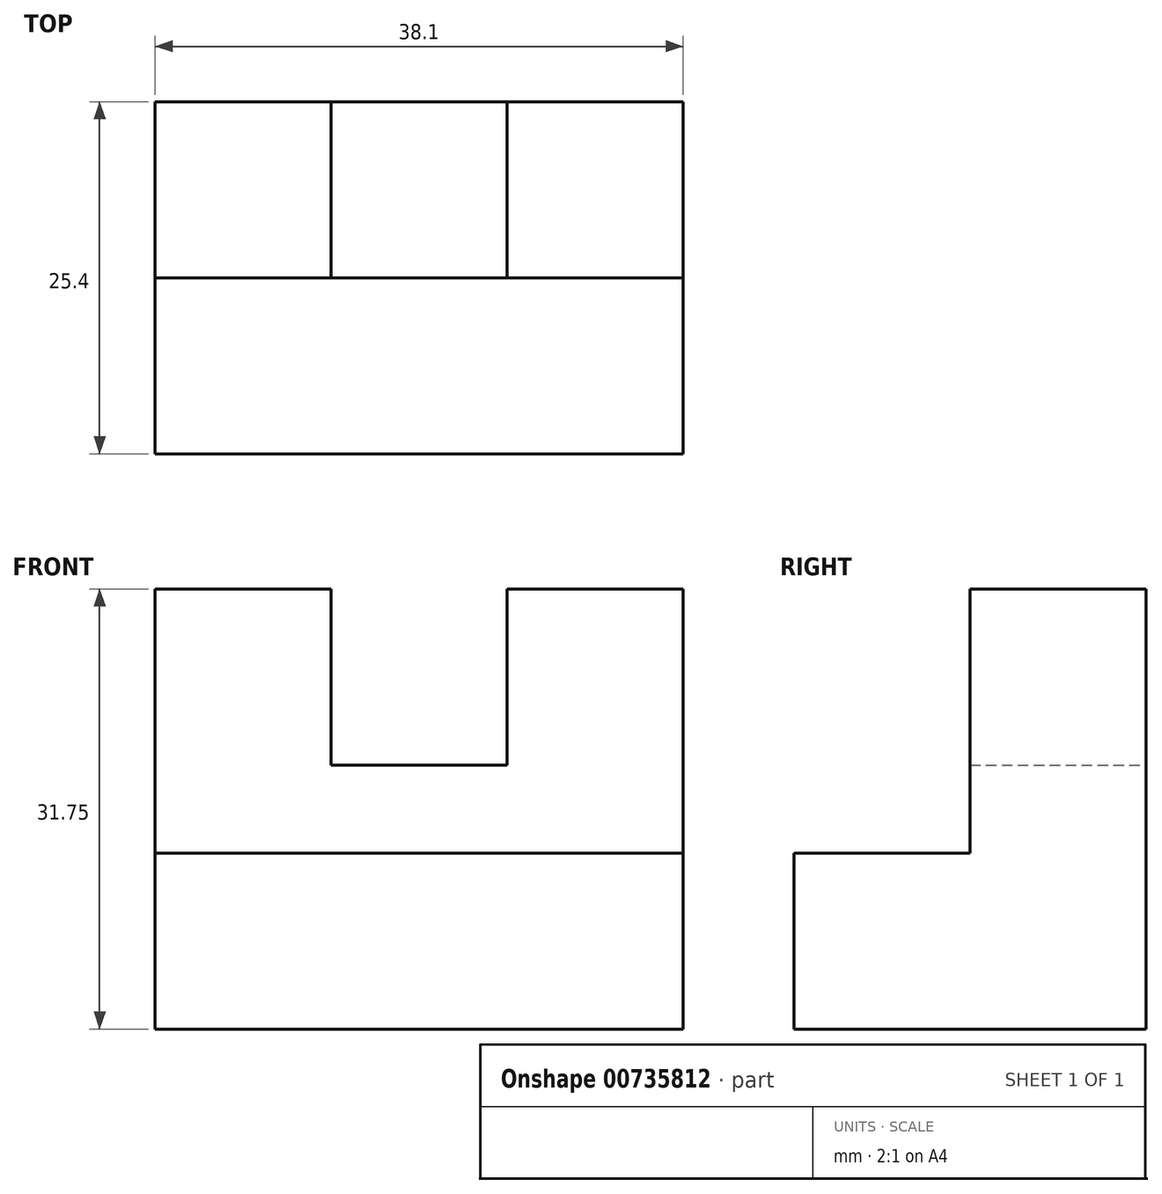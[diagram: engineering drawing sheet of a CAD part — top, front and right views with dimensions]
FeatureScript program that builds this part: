
annotation { "Feature Type Name" : "Feature", "Feature Type Description" : "" }
export const myFeature = defineFeature(function(context is Context, id is Id, definition is map)
    precondition{}
    {
        {
            var Q0;
            Q0=qCreatedBy(makeId("Right.planeOp"),FACE);
            var sketch = newSketch(context, id + "F0", { "sketchPlane" : qUnion([Q0])});
            skLineSegment(sketch, "E0", {"start": v(0, 0) * mm, "end": v(0, 31.75) * mm});
            skLineSegment(sketch, "E1", {"start": v(0, 31.75) * mm, "end": v(-12.7, 31.75) * mm});
            skLineSegment(sketch, "E2", {"start": v(-12.7, 31.75) * mm, "end": v(-12.7, 12.7) * mm});
            skLineSegment(sketch, "E3", {"start": v(-12.7, 12.7) * mm, "end": v(-25.4, 12.7) * mm});
            skLineSegment(sketch, "E4", {"start": v(-25.4, 12.7) * mm, "end": v(-25.4, 0) * mm});
            skLineSegment(sketch, "E5", {"start": v(-25.4, 0) * mm, "end": v(0, 0) * mm});
            skSolve(sketch);
        }
        {
            var Q0;
            Q0=makeQuery(id+"F0.imprint","IMPRINT",FACE,{"disambiguationData":[TD([[makeQuery(id+"F0.imprint","IMPRINT",EDGE,{"derivedFrom":sQuery(id+"F0.wireOp",EDGE,"E0")}),1.0]])]});
            extrude(context, id + "F1", {"entities" : qUnion([Q0]), "depth" : 38.1 * mm, "offsetDistance" : 25.4 * mm});
        }
        {
            var Q0;
            Q0=qCreatedBy(makeId("Front.planeOp"),FACE);
            var sketch = newSketch(context, id + "F2", { "sketchPlane" : qUnion([Q0])});
            skLineSegment(sketch, "E6.bottom", {"start": v(12.7, 31.75) * mm, "end": v(25.4, 31.75) * mm});
            skLineSegment(sketch, "E6.top", {"start": v(12.7, 19.05) * mm, "end": v(25.4, 19.05) * mm});
            skLineSegment(sketch, "E6.left", {"start": v(12.7, 31.75) * mm, "end": v(12.7, 19.05) * mm});
            skLineSegment(sketch, "E6.right", {"start": v(25.4, 31.75) * mm, "end": v(25.4, 19.05) * mm});
            skSolve(sketch);
        }
        {
            var Q0;
            Q0 = qSketchRegion(id + "F2", true);
            extrude(context, id + "F3", {"entities" : qUnion([Q0]), "operationType" : NewBodyOperationType.REMOVE, "depth" : 228.6 * mm, "offsetDistance" : 25.4 * mm});
        }
    });
